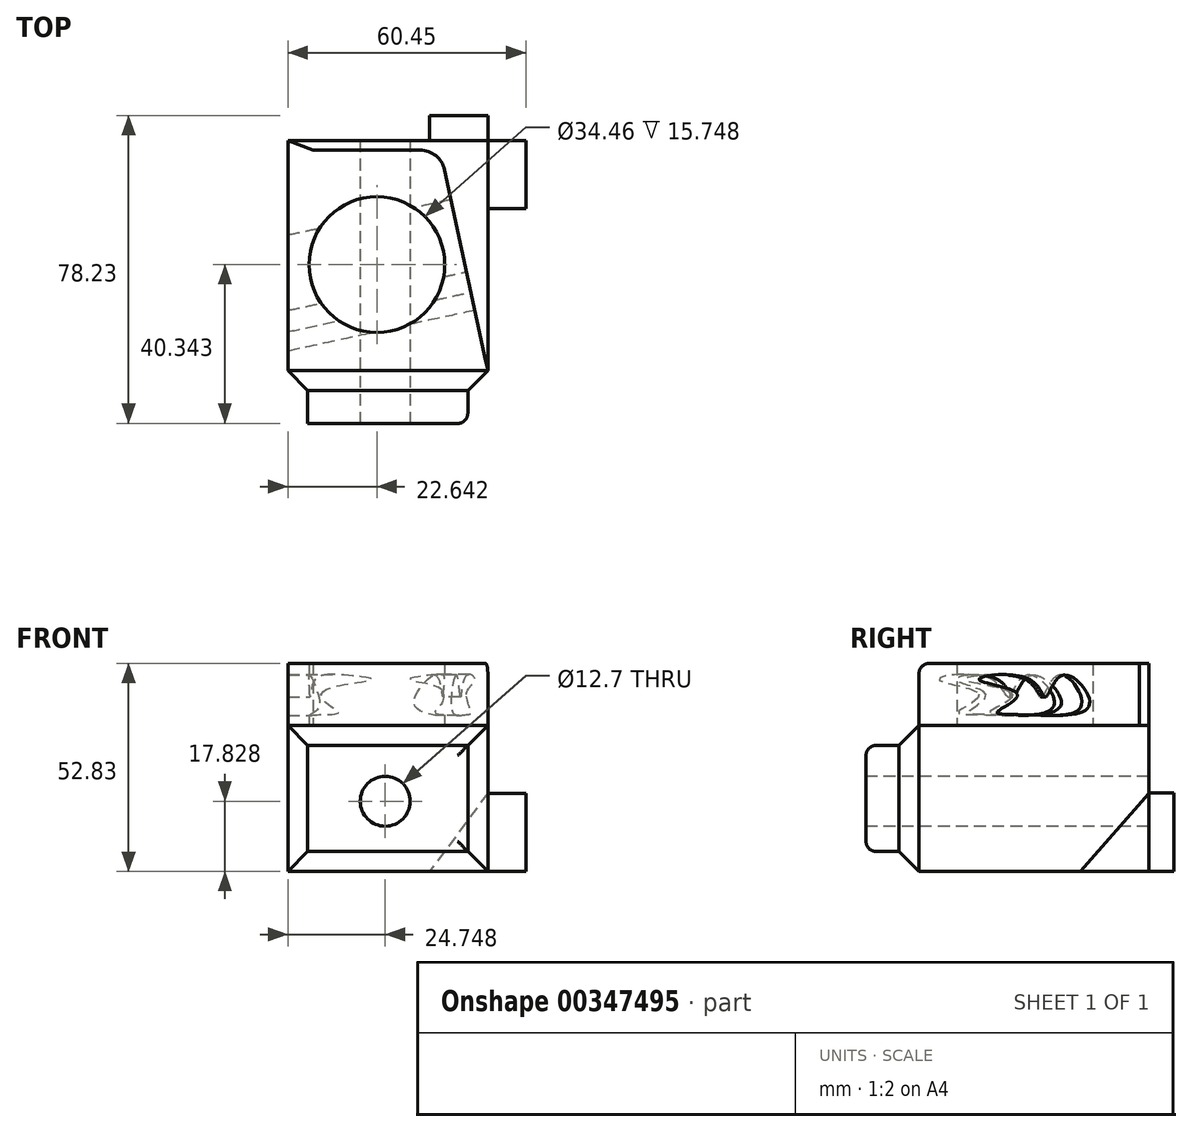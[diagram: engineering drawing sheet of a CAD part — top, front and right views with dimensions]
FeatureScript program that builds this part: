
annotation { "Feature Type Name" : "Feature", "Feature Type Description" : "" }
export const myFeature = defineFeature(function(context is Context, id is Id, definition is map)
    precondition{}
    {
        {
            var Q0;
            Q0=qCreatedBy(makeId("Top.planeOp"),FACE);
            var sketch = newSketch(context, id + "F0", { "sketchPlane" : qUnion([Q0])});
            skLineSegment(sketch, "E0.bottom", {"start": v(-11.97, -37.04) * mm, "end": v(38.83, -37.04) * mm});
            skLineSegment(sketch, "E0.top", {"start": v(-11.97, 26.46) * mm, "end": v(38.83, 26.46) * mm});
            skLineSegment(sketch, "E0.left", {"start": v(-11.97, -37.04) * mm, "end": v(-11.97, 26.46) * mm});
            skLineSegment(sketch, "E0.right", {"start": v(38.83, -37.04) * mm, "end": v(38.83, 26.46) * mm});
            skSolve(sketch);
        }
        {
            var Q0;
            Q0 = qSketchRegion(id + "F0", true);
            extrude(context, id + "F1", {"entities" : qUnion([Q0]), "depth" : 37.08 * mm});
        }
        {
            var Q0;
            Q0=makeQuery(id+"F1.opExtrude","CAP_EDGE",EDGE,{"disambiguationData":[OSD([sQuery(id+"F0.wireOp",EDGE,"E0.bottom")])],"isStart":false});
            var Q1;
            Q1=makeQuery(id+"F1.opExtrude","SWEPT_FACE",FACE,{"disambiguationData":[OSD([sQuery(id+"F0.wireOp",EDGE,"E0.bottom")])]});
            chamfer(context, id + "F2", {"entities" : qUnion([Q0, Q1]), "width" : 5.08 * mm, "tangentPropagation" : true});
        }
        {
            var Q0;
            Q0=makeQuery(id+"F1.opExtrude","SWEPT_FACE",FACE,{"disambiguationData":[OSD([sQuery(id+"F0.wireOp",EDGE,"E0.bottom")])]});
            extrude(context, id + "F3", {"entities" : qUnion([Q0]), "operationType" : NewBodyOperationType.ADD, "depth" : 8.38 * mm});
        }
        {
            var Q0;
            Q0=makeQuery(id+"F3.opExtrude","CAP_FACE",FACE,{"disambiguationData":[OSD([sQuery(id+"F0.wireOp",EDGE,"E0.bottom")])],"isStart":false});
            var sketch = newSketch(context, id + "F4", { "sketchPlane" : qUnion([Q0])});
            skCircle(sketch, "E1", {"center": v(12.78, 17.83) * mm, "radius": 6.35 * mm});
            skSolve(sketch);
        }
        {
            var Q0;
            Q0=makeQuery(id+"F4.imprint","IMPRINT",FACE,{"disambiguationData":[TD([[makeQuery(id+"F4.imprint","IMPRINT",EDGE,{"derivedFrom":sQuery(id+"F4.wireOp",EDGE,"E1")}),1.0]])]});
            extrude(context, id + "F5", {"entities" : qUnion([Q0]), "operationType" : NewBodyOperationType.REMOVE, "depth" : 7.37 * mm});
        }
        {
            var Q0;
            Q0=makeQuery(id+"F1.opExtrude","CAP_FACE",FACE,{"disambiguationData":[OSD([sQuery(id+"F0.wireOp",EDGE,"E0.bottom"),sQuery(id+"F0.wireOp",EDGE,"E0.top"),sQuery(id+"F0.wireOp",EDGE,"E0.left"),sQuery(id+"F0.wireOp",EDGE,"E0.right")])],"isStart":false});
            var sketch = newSketch(context, id + "F6", { "sketchPlane" : qUnion([Q0])});
            skLineSegment(sketch, "E2", {"start": v(-11.97, 26.46) * mm, "end": v(-5.52, 24) * mm});
            skLineSegment(sketch, "E3", {"start": v(-5.52, 24) * mm, "end": v(21.63, 24) * mm});
            skLineSegment(sketch, "E4", {"start": v(27.84, 19) * mm, "end": v(38.83, -31.96) * mm});
            skCircle(sketch, "E5", {"center": v(10.67, -5.08) * mm, "radius": 17.23 * mm});
            skPoint(sketch, "E6.visualSharp", {"position": v(26.76, 24) * mm});
            skArc(sketch, "E6.filletArc", {"start": v(27.84, 19) * mm, "mid": v(25.62, 22.6) * mm, "end": v(21.63, 24) * mm});
            skSolve(sketch);
        }
        {
            var Q0;
            Q0=makeQuery(id+"F6.imprint","IMPRINT",FACE,{"disambiguationData":[TD([[makeQuery(id+"F6.imprint","IMPRINT",EDGE,{"derivedFrom":sQuery(id+"F6.wireOp",EDGE,"E2")}),-1.0]])]});
            extrude(context, id + "F7", {"entities" : qUnion([Q0]), "operationType" : NewBodyOperationType.ADD, "depth" : 15.75 * mm});
        }
        {
            var Q0;
            Q0=makeQuery(id+"F7.opExtrude","CAP_EDGE",EDGE,{"disambiguationData":[OSD([sQuery(id+"F0.wireOp",EDGE,"E0.bottom"),sQuery(id+"F0.wireOp",EDGE,"E0.top"),sQuery(id+"F0.wireOp",EDGE,"E0.left"),sQuery(id+"F0.wireOp",EDGE,"E0.right")])],"isStart":false});
            fillet(context, id + "F8", {"entities" : qUnion([Q0]), "radius" : 2.54 * mm, "tangentPropagation" : true, "allowEdgeOverflow" : false});
        }
        {
            var Q0;
            Q0=makeQuery(id+"F4.imprint","IMPRINT",FACE,{"disambiguationData":[TD([[makeQuery(id+"F4.imprint","IMPRINT",EDGE,{"derivedFrom":sQuery(id+"F4.wireOp",EDGE,"E1")}),1.0]])]});
            extrude(context, id + "F9", {"entities" : qUnion([Q0]), "operationType" : NewBodyOperationType.REMOVE, "oppositeDirection" : true, "depth" : 95.25 * mm});
        }
        {
            var Q0;
            {var subQ0=sQuery(id+"F0.wireOp",EDGE,"E0.bottom");Q0=makeQuery(id+"F3.opExtrude","CAP_EDGE",EDGE,{"disambiguationData":[OSD([subQ0]),TDD([makeQuery(id+"F2.opChamfer","BLEND_EDGE",EDGE,{"blendedFrom":[makeQuery(id+"F1.opExtrude","CAP_EDGE",EDGE,{"disambiguationData":[OSD([subQ0])],"isStart":false}),makeQuery(id+"F1.opExtrude","SWEPT_FACE",FACE,{"disambiguationData":[OSD([subQ0])]})],"blendedInto":[makeQuery(id+"F1.opExtrude","SWEPT_FACE",FACE,{"disambiguationData":[OSD([subQ0])]})]})])],"isStart":false});}
            var Q1;
            {var subQ0=sQuery(id+"F0.wireOp",EDGE,"E0.bottom");Q1=makeQuery(id+"F3.opExtrude","CAP_EDGE",EDGE,{"disambiguationData":[OSD([subQ0]),TDD([makeQuery(id+"F2.opChamfer","BLEND_EDGE",EDGE,{"blendedFrom":[makeQuery(id+"F1.opExtrude","CAP_EDGE",EDGE,{"disambiguationData":[OSD([subQ0])],"isStart":true}),makeQuery(id+"F1.opExtrude","SWEPT_FACE",FACE,{"disambiguationData":[OSD([subQ0])]})],"blendedInto":[makeQuery(id+"F1.opExtrude","SWEPT_FACE",FACE,{"disambiguationData":[OSD([subQ0])]})]})])],"isStart":false});}
            var Q2;
            Q2=makeQuery(id+"F3.opExtrude","CAP_EDGE",EDGE,{"disambiguationData":[OSD([sQuery(id+"F0.wireOp",EDGE,"E0.bottom"),sQuery(id+"F0.wireOp",EDGE,"E0.right")])],"isStart":false});
            fillet(context, id + "F10", {"entities" : qUnion([Q0, Q1, Q2]), "radius" : 2.54 * mm, "tangentPropagation" : true, "allowEdgeOverflow" : false});
        }
        {
            var Q0;
            Q0=makeQuery(id+"F7.opExtrude","SWEPT_FACE",FACE,{"disambiguationData":[OSD([sQuery(id+"F6.wireOp",EDGE,"E4")])]});
            var sketch = newSketch(context, id + "F11", { "sketchPlane" : qUnion([Q0])});
            skFitSpline(sketch, "E7", {"points": [v(-13.84, 44.96) * mm, v(-23.78, 48.7) * mm, v(-10.56, 48.7) * mm, v(-6.46, 44.37) * mm, v(-1.9, 49.87) * mm, v(4.88, 42.38) * mm, v(-12.89, 39.83) * mm, v(-18.98, 40.63) * mm, v(-13.84, 44.96) * mm]});
            skSolve(sketch);
        }
        {
            var Q0;
            Q0=makeQuery(id+"F11.imprint","IMPRINT",FACE,{"disambiguationData":[TD([[makeQuery(id+"F11.imprint","IMPRINT",EDGE,{"derivedFrom":sQuery(id+"F11.wireOp",EDGE,"E7")}),-1.0]])]});
            extrude(context, id + "F12", {"entities" : qUnion([Q0]), "operationType" : NewBodyOperationType.REMOVE, "oppositeDirection" : true, "depth" : 64.52 * mm});
        }
        {
            var Q0;
            Q0=makeQuery(id+"F1.opExtrude","SWEPT_FACE",FACE,{"disambiguationData":[OSD([sQuery(id+"F0.wireOp",EDGE,"E0.right")])]});
            var sketch = newSketch(context, id + "F13", { "sketchPlane" : qUnion([Q0])});
            skLineSegment(sketch, "E8", {"start": v(26.46, 19.85) * mm, "end": v(9.1, 0) * mm});
            skSolve(sketch);
        }
        {
            var Q0;
            Q0=makeQuery(id+"F1.opExtrude","SWEPT_FACE",FACE,{"disambiguationData":[OSD([sQuery(id+"F0.wireOp",EDGE,"E0.top")])]});
            var sketch = newSketch(context, id + "F14", { "sketchPlane" : qUnion([Q0])});
            skLineSegment(sketch, "E9", {"start": v(-38.83, 19.89) * mm, "end": v(-24.03, 0) * mm});
            skSolve(sketch);
        }
        {
            var Q0;
            {var subQ0=sQuery(id+"F13.wireOp",EDGE,"E8");Q0=makeQuery(id+"F13.imprint","IMPRINT",FACE,{"disambiguationData":[TD([[makeQuery(id+"F13.imprint","IMPRINT",EDGE,{"derivedFrom":subQ0}),1.0]])]});}
            extrude(context, id + "F15", {"entities" : qUnion([Q0]), "operationType" : NewBodyOperationType.ADD, "depth" : 9.65 * mm});
        }
        {
            var Q0;
            {var subQ0=sQuery(id+"F14.wireOp",EDGE,"E9");Q0=makeQuery(id+"F14.imprint","IMPRINT",FACE,{"disambiguationData":[TD([[makeQuery(id+"F14.imprint","IMPRINT",EDGE,{"derivedFrom":subQ0}),-1.0]])]});}
            extrude(context, id + "F16", {"entities" : qUnion([Q0]), "operationType" : NewBodyOperationType.ADD, "depth" : 6.35 * mm});
        }
    });
